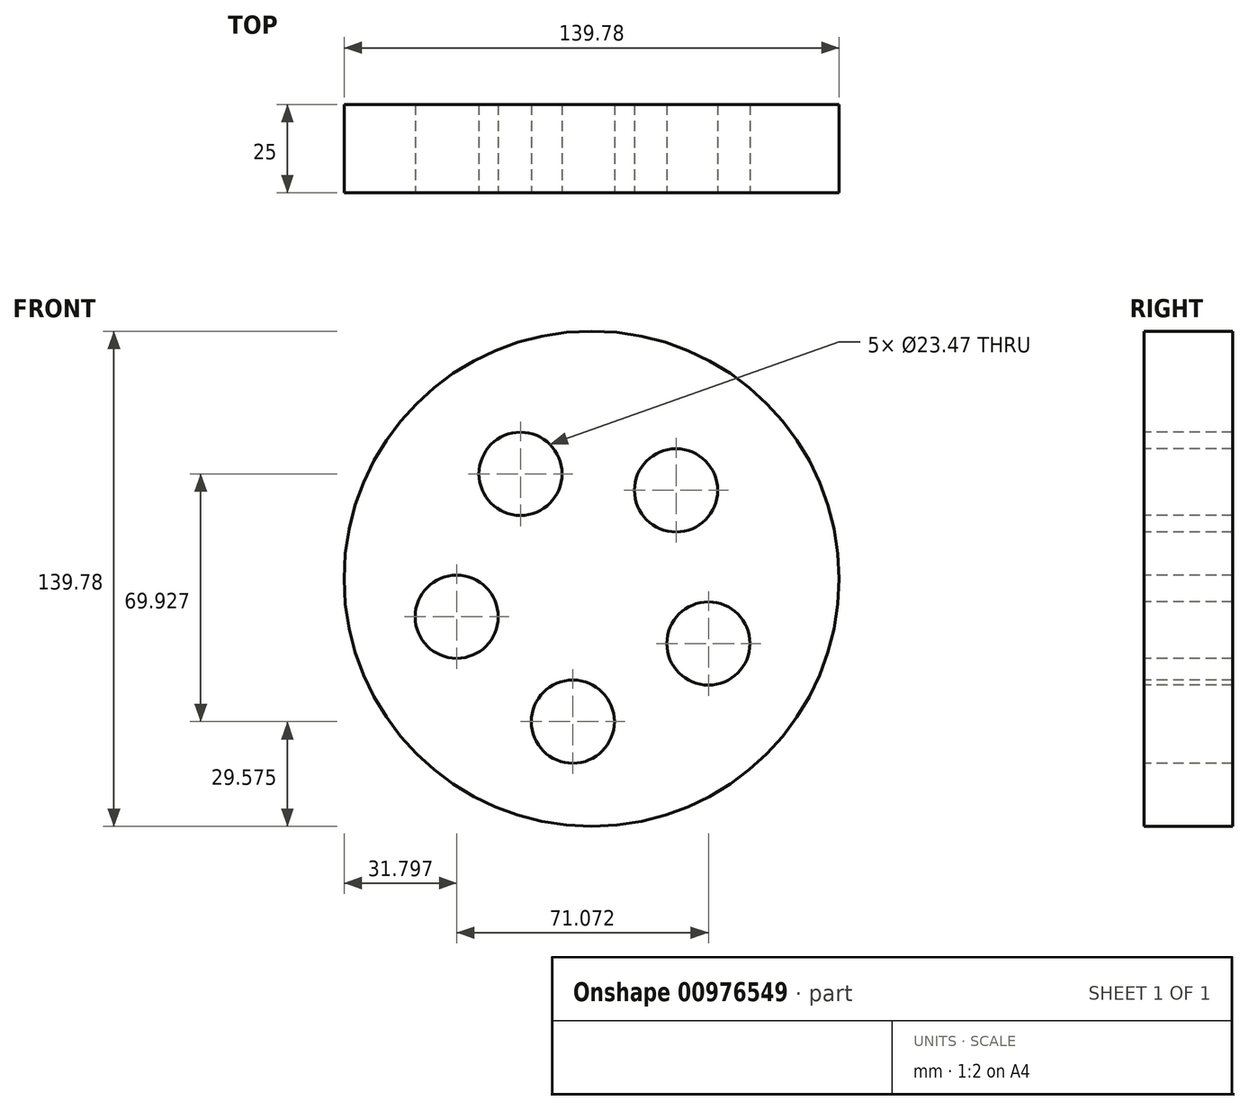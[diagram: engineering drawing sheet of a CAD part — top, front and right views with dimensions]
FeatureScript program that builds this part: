
annotation { "Feature Type Name" : "Feature", "Feature Type Description" : "" }
export const myFeature = defineFeature(function(context is Context, id is Id, definition is map)
    precondition{}
    {
        {
            var Q0;
            Q0=qCreatedBy(makeId("Front.planeOp"),FACE);
            var sketch = newSketch(context, id + "F0", { "sketchPlane" : qUnion([Q0])});
            skCircle(sketch, "E0", {"center": v(-15.67, 14.95) * mm, "radius": 69.89 * mm});
            skSolve(sketch);
        }
        {
            var Q0;
            Q0=makeQuery(id+"F0.imprint","IMPRINT",FACE,{"disambiguationData":[TD([[makeQuery(id+"F0.imprint","IMPRINT",EDGE,{"derivedFrom":sQuery(id+"F0.wireOp",EDGE,"E0")}),1.0]])]});
            extrude(context, id + "F1", {"entities" : qUnion([Q0]), "depth" : 25 * mm, "offsetDistance" : 25 * mm});
        }
        {
            var Q0;
            Q0=makeQuery(id+"F1.opExtrude","CAP_FACE",FACE,{"disambiguationData":[OSD([sQuery(id+"F0.wireOp",EDGE,"E0")])],"isStart":false});
            var sketch = newSketch(context, id + "F2", { "sketchPlane" : qUnion([Q0])});
            skCircle(sketch, "E1", {"center": v(-35.75, 44.56) * mm, "radius": 11.73 * mm});
            skCircle(sketch, "E2.1.0", {"center": v(-53.76, 4.23) * mm, "radius": 11.73 * mm});
            skCircle(sketch, "E2.2.0", {"center": v(-20.97, -25.36) * mm, "radius": 11.73 * mm});
            skCircle(sketch, "E2.3.0", {"center": v(17.3, -3.32) * mm, "radius": 11.73 * mm});
            skCircle(sketch, "E2.4.0", {"center": v(8.17, 39.9) * mm, "radius": 11.73 * mm});
            skPoint(sketch, "E2.center", {"position": v(-17, 12) * mm});
            skSolve(sketch);
        }
        {
            var Q0;
            Q0 = qSketchRegion(id + "F2", true);
            extrude(context, id + "F3", {"entities" : qUnion([Q0]), "operationType" : NewBodyOperationType.REMOVE, "oppositeDirection" : true, "depth" : 77 * mm, "offsetDistance" : 25 * mm});
        }
    });
